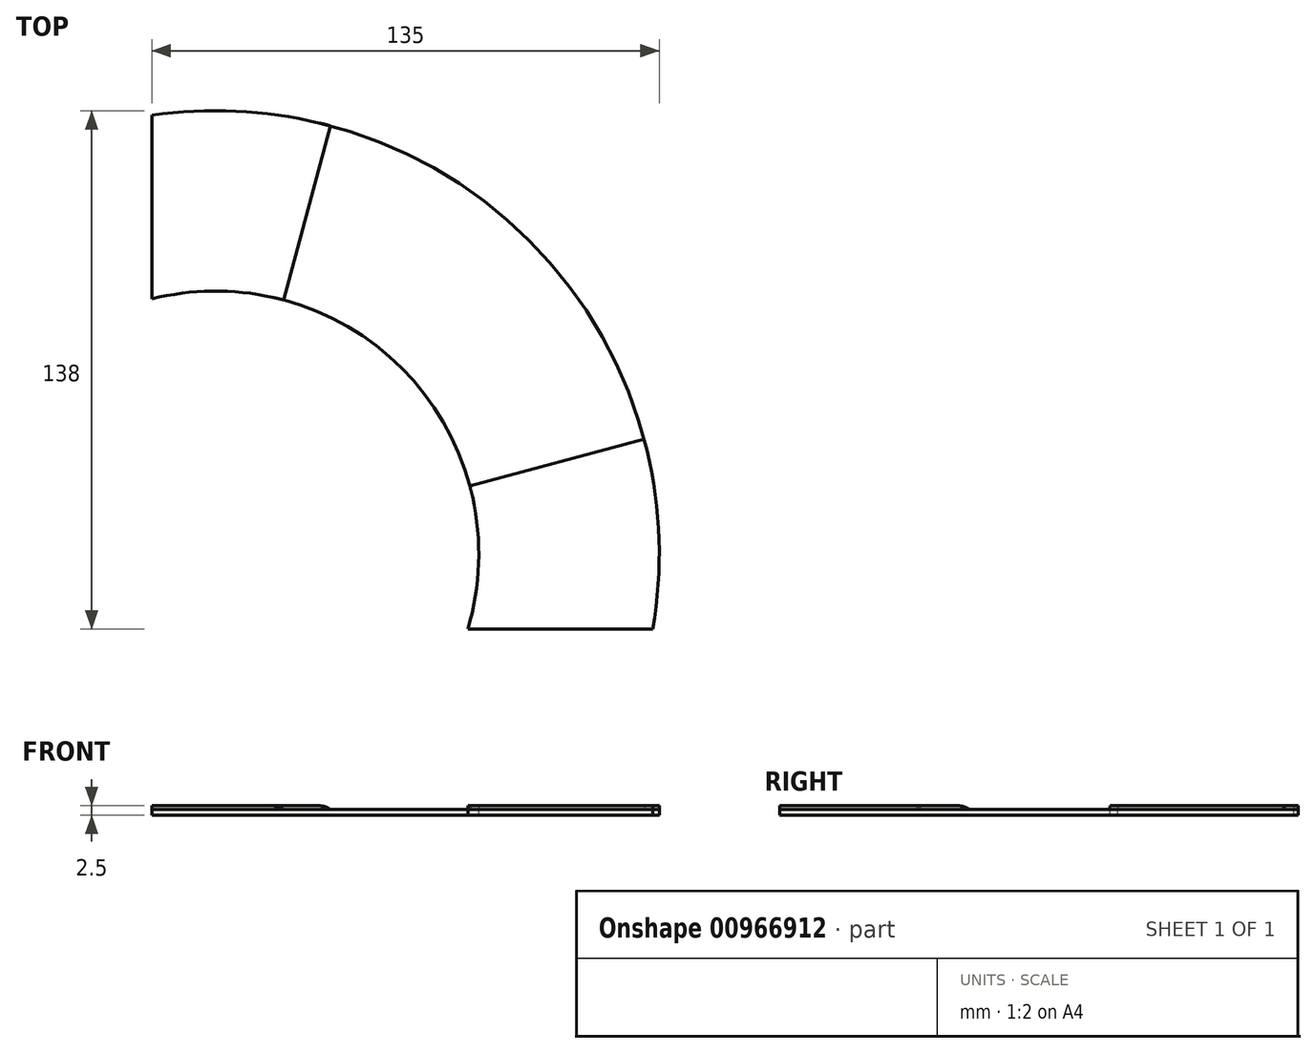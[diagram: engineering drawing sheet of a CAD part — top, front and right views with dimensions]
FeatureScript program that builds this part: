
annotation { "Feature Type Name" : "Feature", "Feature Type Description" : "" }
export const myFeature = defineFeature(function(context is Context, id is Id, definition is map)
    precondition{}
    {
        {
            var Q0;
            Q0=qCreatedBy(makeId("Top.planeOp"),FACE);
            var sketch = newSketch(context, id + "F0", { "sketchPlane" : qUnion([Q0])});
            skArc(sketch, "E0", {"start": v(67.08, -20) * mm, "mid": v(50.59, 48.39) * mm, "end": v(-17, 67.9) * mm});
            skArc(sketch, "E1", {"start": v(116.3, -20) * mm, "mid": v(84.5, 82.36) * mm, "end": v(-17, 116.77) * mm});
            skLineSegment(sketch, "E2.0.0", {"start": v(-17, 67.9) * mm, "end": v(-17, -20) * mm, "construction": true});
            skLineSegment(sketch, "E2.0.1", {"start": v(-17, -20) * mm, "end": v(67.08, -20) * mm, "construction": true});
            skLineSegment(sketch, "E3", {"start": v(67.08, -20) * mm, "end": v(116.3, -20) * mm});
            skLineSegment(sketch, "E4", {"start": v(-17, 67.9) * mm, "end": v(-17, 116.77) * mm});
            skLineSegment(sketch, "E5", {"start": v(67.61, 18.12) * mm, "end": v(113.98, 30.54) * mm});
            skLineSegment(sketch, "E6", {"start": v(30.54, 113.98) * mm, "end": v(18.12, 67.61) * mm});
            skSolve(sketch);
        }
        {
            var Q0;
            {var subQ0=sQuery(id+"F0.wireOp",EDGE,"E4");Q0=makeQuery(id+"F0.imprint","IMPRINT",FACE,{"disambiguationData":[TD([[makeQuery(id+"F0.imprint","IMPRINT",EDGE,{"derivedFrom":subQ0}),-1.0]])]});}
            var Q1;
            {var subQ0=sQuery(id+"F0.wireOp",EDGE,"E3");Q1=makeQuery(id+"F0.imprint","IMPRINT",FACE,{"disambiguationData":[TD([[makeQuery(id+"F0.imprint","IMPRINT",EDGE,{"derivedFrom":subQ0}),1.0]])]});}
            extrude(context, id + "F1", {"entities" : qUnion([Q0, Q1]), "depth" : 1 * mm, "offsetDistance" : 25 * mm});
        }
        {
            var Q0;
            {var subQ0=sQuery(id+"F0.wireOp",EDGE,"E4");Q0=makeQuery(id+"F0.imprint","IMPRINT",FACE,{"disambiguationData":[TD([[makeQuery(id+"F0.imprint","IMPRINT",EDGE,{"derivedFrom":subQ0}),-1.0]])]});}
            var Q1;
            {var subQ0=sQuery(id+"F0.wireOp",EDGE,"E5");Q1=makeQuery(id+"F0.imprint","IMPRINT",FACE,{"disambiguationData":[TD([[makeQuery(id+"F0.imprint","IMPRINT",EDGE,{"derivedFrom":subQ0}),1.0]])]});}
            var Q2;
            {var subQ0=sQuery(id+"F0.wireOp",EDGE,"E3");Q2=makeQuery(id+"F0.imprint","IMPRINT",FACE,{"disambiguationData":[TD([[makeQuery(id+"F0.imprint","IMPRINT",EDGE,{"derivedFrom":subQ0}),1.0]])]});}
            var Q3;
            Q3=makeQuery(id+"F1.opExtrude","CAP_VERTEX",VERTEX,{"disambiguationData":[OSD([sQuery(id+"F0.wireOp",EDGE,"E1"),sQuery(id+"F0.wireOp",EDGE,"E6")])],"isStart":false});
            extrude(context, id + "F2", {"entities" : qUnion([Q0, Q1, Q2]), "oppositeDirection" : true, "depth" : 1.5 * mm, "offsetDistance" : 25 * mm});
        }
        {
            var Q0;
            Q0=makeQuery(id+"F1.opExtrude","CAP_EDGE",EDGE,{"disambiguationData":[OSD([sQuery(id+"F0.wireOp",EDGE,"E5")])],"isStart":false});
            var Q1;
            Q1=makeQuery(id+"F1.opExtrude","CAP_EDGE",EDGE,{"disambiguationData":[OSD([sQuery(id+"F0.wireOp",EDGE,"E6")])],"isStart":false});
            chamfer(context, id + "F3", {"entities" : qUnion([Q0, Q1]), "width" : 1 * mm, "tangentPropagation" : true});
        }
        {
            var Q0;
            {var subQ0=sQuery(id+"F0.wireOp",EDGE,"E5");Q0=makeQuery(id+"F3.opChamfer","BLEND_EDGE",EDGE,{"blendedFrom":[makeQuery(id+"F1.opExtrude","CAP_EDGE",EDGE,{"disambiguationData":[OSD([subQ0])],"isStart":false}),makeQuery(id+"F1.opExtrude","CAP_FACE",FACE,{"disambiguationData":[OSD([sQuery(id+"F0.wireOp",EDGE,"E0"),sQuery(id+"F0.wireOp",EDGE,"E1"),sQuery(id+"F0.wireOp",EDGE,"E3"),subQ0])],"isStart":false})],"blendedInto":[makeQuery(id+"F1.opExtrude","CAP_FACE",FACE,{"disambiguationData":[OSD([sQuery(id+"F0.wireOp",EDGE,"E0"),sQuery(id+"F0.wireOp",EDGE,"E1"),sQuery(id+"F0.wireOp",EDGE,"E3"),subQ0])],"isStart":false})]});}
            var Q1;
            {var subQ0=sQuery(id+"F0.wireOp",EDGE,"E6");Q1=makeQuery(id+"F3.opChamfer","BLEND_EDGE",EDGE,{"blendedFrom":[makeQuery(id+"F1.opExtrude","CAP_EDGE",EDGE,{"disambiguationData":[OSD([subQ0])],"isStart":false}),makeQuery(id+"F1.opExtrude","CAP_FACE",FACE,{"disambiguationData":[OSD([sQuery(id+"F0.wireOp",EDGE,"E0"),sQuery(id+"F0.wireOp",EDGE,"E1"),sQuery(id+"F0.wireOp",EDGE,"E4"),subQ0])],"isStart":false})],"blendedInto":[makeQuery(id+"F1.opExtrude","CAP_FACE",FACE,{"disambiguationData":[OSD([sQuery(id+"F0.wireOp",EDGE,"E0"),sQuery(id+"F0.wireOp",EDGE,"E1"),sQuery(id+"F0.wireOp",EDGE,"E4"),subQ0])],"isStart":false})]});}
            fillet(context, id + "F4", {"entities" : qUnion([Q0, Q1]), "radius" : 5 * mm, "tangentPropagation" : true, "allowEdgeOverflow" : false});
        }
    });
